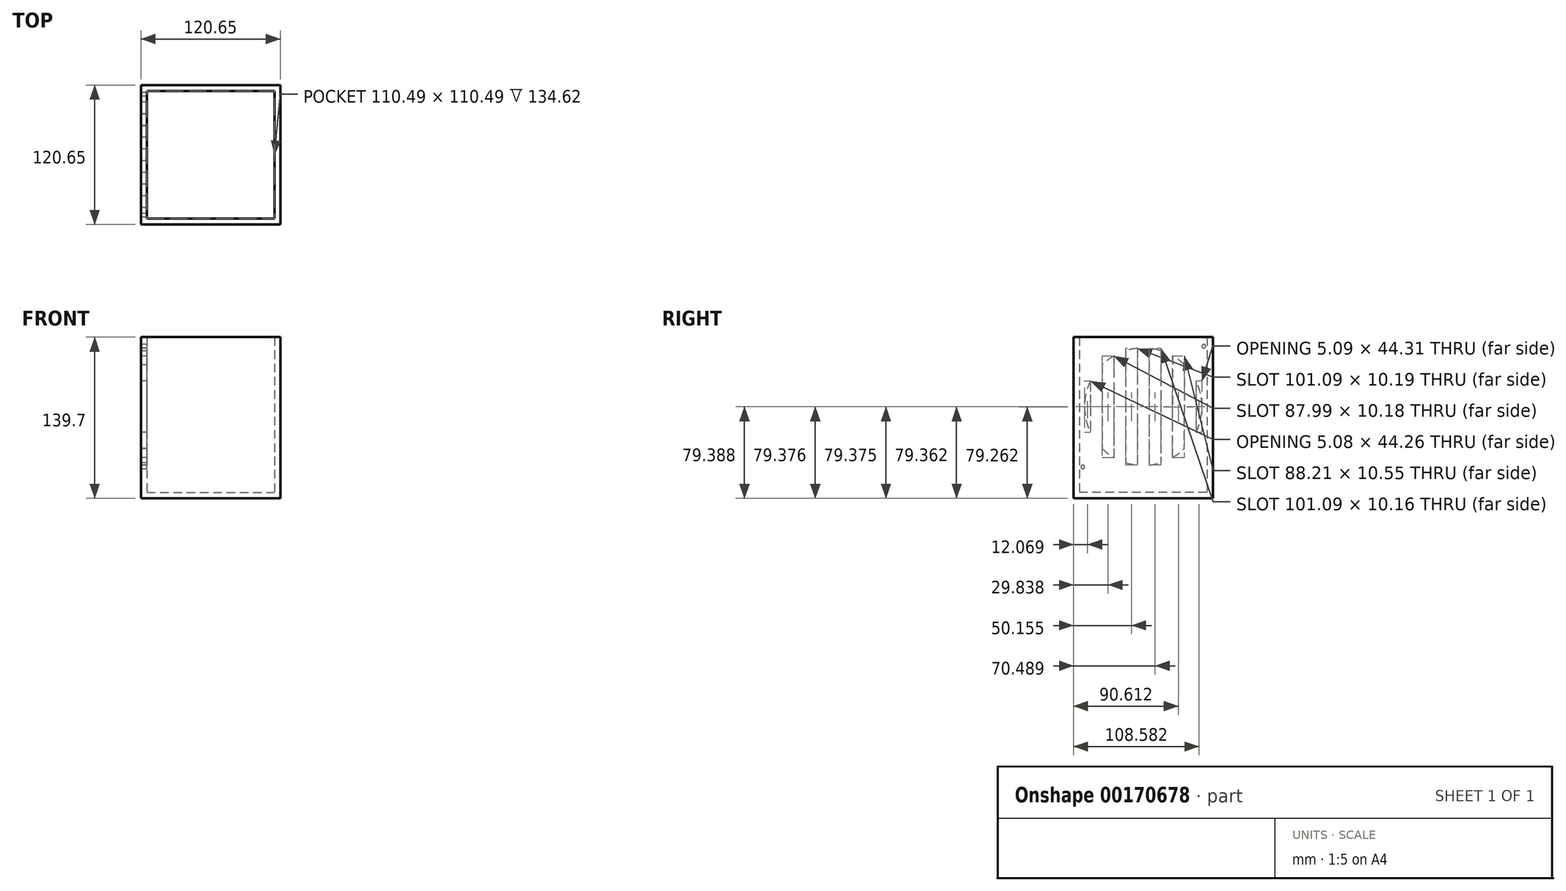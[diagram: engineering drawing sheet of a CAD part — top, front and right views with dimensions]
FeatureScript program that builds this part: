
annotation { "Feature Type Name" : "Feature", "Feature Type Description" : "" }
export const myFeature = defineFeature(function(context is Context, id is Id, definition is map)
    precondition{}
    {
        {
            var Q0;
            Q0=qCreatedBy(makeId("Top.planeOp"),FACE);
            var sketch = newSketch(context, id + "F0", { "sketchPlane" : qUnion([Q0])});
            skLineSegment(sketch, "E0.bottom", {"start": v(-81.61, 78.05) * mm, "end": v(39.04, 78.05) * mm});
            skLineSegment(sketch, "E0.top", {"start": v(-81.61, -42.6) * mm, "end": v(39.04, -42.6) * mm});
            skLineSegment(sketch, "E0.left", {"start": v(-81.61, 78.05) * mm, "end": v(-81.61, -42.6) * mm});
            skLineSegment(sketch, "E0.right", {"start": v(39.04, 78.05) * mm, "end": v(39.04, -42.6) * mm});
            skSolve(sketch);
        }
        {
            var Q0;
            Q0=makeQuery(id+"F0.imprint","IMPRINT",FACE,{"disambiguationData":[TD([[makeQuery(id+"F0.imprint","IMPRINT",EDGE,{"derivedFrom":sQuery(id+"F0.wireOp",EDGE,"E0.bottom")}),-1.0]])]});
            extrude(context, id + "F1", {"entities" : qUnion([Q0]), "depth" : 139.7 * mm});
        }
        {
            var Q0;
            Q0=makeQuery(id+"F1.opExtrude","CAP_FACE",FACE,{"disambiguationData":[OSD([sQuery(id+"F0.wireOp",EDGE,"E0.bottom"),sQuery(id+"F0.wireOp",EDGE,"E0.top"),sQuery(id+"F0.wireOp",EDGE,"E0.left"),sQuery(id+"F0.wireOp",EDGE,"E0.right")])],"isStart":false});
            shell(context, id + "F2", {"entities" : qUnion([Q0]), "thickness" : 5.08 * mm});
        }
        {
            var Q0;
            Q0=makeQuery(id+"F1.opExtrude","SWEPT_FACE",FACE,{"disambiguationData":[OSD([sQuery(id+"F0.wireOp",EDGE,"E0.left")])]});
            var sketch = newSketch(context, id + "F3", { "sketchPlane" : qUnion([Q0])});
            skCircle(sketch, "E1", {"center": v(-17.73, 79.38) * mm, "radius": 50.8 * mm});
            skPoint(sketch, "E1.centerSnap0", {"position": v(-17.73, 139.7) * mm});
            skLineSegment(sketch, "E2", {"start": v(-17.73, 130.18) * mm, "end": v(-17.7, 28.58) * mm});
            skPoint(sketch, "E3.startSnap0", {"position": v(-20.19, 79.42) * mm});
            skLineSegment(sketch, "E4", {"start": v(-17.73, 79.38) * mm, "end": v(-12.65, 79.38) * mm});
            skLineSegment(sketch, "E5", {"start": v(-12.65, 79.38) * mm, "end": v(-22.8, 79.42) * mm});
            skLineSegment(sketch, "E6", {"start": v(-22.8, 129.92) * mm, "end": v(-22.8, 28.83) * mm});
            skLineSegment(sketch, "E7", {"start": v(-12.65, 129.92) * mm, "end": v(-12.62, 28.83) * mm});
            skLineSegment(sketch, "E8", {"start": v(-22.8, 79.42) * mm, "end": v(-32.97, 79.42) * mm});
            skLineSegment(sketch, "E9", {"start": v(-32.97, 79.42) * mm, "end": v(-43.13, 79.42) * mm});
            skLineSegment(sketch, "E10", {"start": v(-43.13, 79.42) * mm, "end": v(-53.29, 79.38) * mm});
            skLineSegment(sketch, "E11", {"start": v(-53.29, 79.38) * mm, "end": v(-63.45, 79.37) * mm});
            skLineSegment(sketch, "E12", {"start": v(-63.45, 79.37) * mm, "end": v(-68.53, 79.37) * mm});
            skLineSegment(sketch, "E13", {"start": v(33.07, 79.38) * mm, "end": v(28, 79.38) * mm});
            skLineSegment(sketch, "E14", {"start": v(28, 79.38) * mm, "end": v(17.83, 79.37) * mm});
            skLineSegment(sketch, "E15", {"start": v(17.83, 79.37) * mm, "end": v(7.67, 79.37) * mm});
            skLineSegment(sketch, "E16", {"start": v(7.67, 79.37) * mm, "end": v(-2.49, 79.37) * mm});
            skLineSegment(sketch, "E17", {"start": v(-2.49, 79.37) * mm, "end": v(-12.65, 79.38) * mm});
            skLineSegment(sketch, "E18", {"start": v(-32.97, 127.84) * mm, "end": v(-32.97, 30.91) * mm});
            skLineSegment(sketch, "E19", {"start": v(-43.13, 123.37) * mm, "end": v(-42.73, 35.16) * mm});
            skLineSegment(sketch, "E20", {"start": v(-53.29, 115.65) * mm, "end": v(-52.96, 42.78) * mm});
            skLineSegment(sketch, "E21", {"start": v(-63.45, 101.52) * mm, "end": v(-63.44, 57.2) * mm});
            skLineSegment(sketch, "E22", {"start": v(-2.49, 127.84) * mm, "end": v(-2.46, 30.92) * mm});
            skLineSegment(sketch, "E23", {"start": v(7.67, 123.37) * mm, "end": v(7.67, 35.38) * mm});
            skLineSegment(sketch, "E24", {"start": v(17.83, 115.65) * mm, "end": v(17.85, 43.12) * mm});
            skLineSegment(sketch, "E25", {"start": v(28, 101.52) * mm, "end": v(28, 57.26) * mm});
            skSolve(sketch);
        }
        {
            var Q0;
            {var subQ5=sQuery(id+"F3.wireOp",EDGE,"E8");Q0=makeQuery(id+"F3.imprint","IMPRINT",FACE,{"disambiguationData":[TD([[makeQuery(id+"F3.imprint","IMPRINT",EDGE,{"derivedFrom":subQ5}),-1.0]])]});}
            var Q1;
            {var subQ5=sQuery(id+"F3.wireOp",EDGE,"E8");Q1=makeQuery(id+"F3.imprint","IMPRINT",FACE,{"disambiguationData":[TD([[makeQuery(id+"F3.imprint","IMPRINT",EDGE,{"derivedFrom":subQ5}),1.0]])]});}
            var Q2;
            {var subQ5=sQuery(id+"F3.wireOp",EDGE,"E7");var subQ6=sQuery(id+"F3.wireOp",EDGE,"E1");var subQ7=makeQuery(id+"F3.imprint","INTERSECT",VERTEX,{"disambiguationData":[OD(1.0)],"derivedFrom":[subQ6,subQ5]});Q2=makeQuery(id+"F3.imprint","IMPRINT",FACE,{"disambiguationData":[TD([[makeQuery(id+"F3.imprint","IMPRINT",EDGE,{"disambiguationData":[TD([[subQ7,-1.0]])],"derivedFrom":subQ6}),1.0]])]});}
            var Q3;
            {var subQ3=sQuery(id+"F3.wireOp",EDGE,"E7");var subQ6=sQuery(id+"F3.wireOp",EDGE,"E1");var subQ9=makeQuery(id+"F3.imprint","INTERSECT",VERTEX,{"disambiguationData":[OD(0.0)],"derivedFrom":[subQ6,subQ3]});Q3=makeQuery(id+"F3.imprint","IMPRINT",FACE,{"disambiguationData":[TD([[makeQuery(id+"F3.imprint","IMPRINT",EDGE,{"disambiguationData":[TD([[subQ9,1.0]])],"derivedFrom":subQ6}),1.0]])]});}
            var Q4;
            {var subQ0=sQuery(id+"F3.wireOp",EDGE,"E15");Q4=makeQuery(id+"F3.imprint","IMPRINT",FACE,{"disambiguationData":[TD([[makeQuery(id+"F3.imprint","IMPRINT",EDGE,{"derivedFrom":subQ0}),-1.0]])]});}
            var Q5;
            {var subQ1=sQuery(id+"F3.wireOp",EDGE,"E15");Q5=makeQuery(id+"F3.imprint","IMPRINT",FACE,{"disambiguationData":[TD([[makeQuery(id+"F3.imprint","IMPRINT",EDGE,{"derivedFrom":subQ1}),1.0]])]});}
            var Q6;
            {var subQ0=sQuery(id+"F3.wireOp",EDGE,"E13");var subQ1=sQuery(id+"F3.wireOp",EDGE,"E1");var subQ2=makeQuery(id+"F3.imprint","INTERSECT",VERTEX,{"derivedFrom":[subQ1,subQ0]});Q6=makeQuery(id+"F3.imprint","IMPRINT",FACE,{"disambiguationData":[TD([[makeQuery(id+"F3.imprint","IMPRINT",EDGE,{"disambiguationData":[TD([[subQ2,-1.0]])],"derivedFrom":subQ1}),1.0]])]});}
            var Q7;
            {var subQ0=sQuery(id+"F3.wireOp",EDGE,"E13");var subQ1=sQuery(id+"F3.wireOp",EDGE,"E1");var subQ2=makeQuery(id+"F3.imprint","INTERSECT",VERTEX,{"derivedFrom":[subQ1,subQ0]});Q7=makeQuery(id+"F3.imprint","IMPRINT",FACE,{"disambiguationData":[TD([[makeQuery(id+"F3.imprint","IMPRINT",EDGE,{"disambiguationData":[TD([[subQ2,1.0]])],"derivedFrom":subQ1}),1.0]])]});}
            var Q8;
            {var subQ5=sQuery(id+"F3.wireOp",EDGE,"E19");var subQ6=sQuery(id+"F3.wireOp",EDGE,"E1");var subQ7=makeQuery(id+"F3.imprint","INTERSECT",VERTEX,{"disambiguationData":[OD(0.0)],"derivedFrom":[subQ6,subQ5]});Q8=makeQuery(id+"F3.imprint","IMPRINT",FACE,{"disambiguationData":[TD([[makeQuery(id+"F3.imprint","IMPRINT",EDGE,{"disambiguationData":[TD([[subQ7,-1.0]])],"derivedFrom":subQ6}),1.0]])]});}
            var Q9;
            {var subQ0=sQuery(id+"F3.wireOp",EDGE,"E19");var subQ1=sQuery(id+"F3.wireOp",EDGE,"E1");var subQ2=makeQuery(id+"F3.imprint","INTERSECT",VERTEX,{"disambiguationData":[OD(1.0)],"derivedFrom":[subQ1,subQ0]});Q9=makeQuery(id+"F3.imprint","IMPRINT",FACE,{"disambiguationData":[TD([[makeQuery(id+"F3.imprint","IMPRINT",EDGE,{"disambiguationData":[TD([[subQ2,1.0]])],"derivedFrom":subQ1}),1.0]])]});}
            var Q10;
            {var subQ0=sQuery(id+"F3.wireOp",EDGE,"E12");Q10=makeQuery(id+"F3.imprint","IMPRINT",FACE,{"disambiguationData":[TD([[makeQuery(id+"F3.imprint","IMPRINT",EDGE,{"derivedFrom":subQ0}),-1.0]])]});}
            var Q11;
            {var subQ0=sQuery(id+"F3.wireOp",EDGE,"E12");Q11=makeQuery(id+"F3.imprint","IMPRINT",FACE,{"disambiguationData":[TD([[makeQuery(id+"F3.imprint","IMPRINT",EDGE,{"derivedFrom":subQ0}),1.0]])]});}
            extrude(context, id + "F4", {"entities" : qUnion([Q0, Q1, Q2, Q3, Q4, Q5, Q6, Q7, Q8, Q9, Q10, Q11]), "operationType" : NewBodyOperationType.REMOVE, "oppositeDirection" : true, "depth" : 25.4 * mm});
        }
        {
            var Q0;
            Q0=makeQuery(id+"F1.opExtrude","SWEPT_FACE",FACE,{"disambiguationData":[OSD([sQuery(id+"F0.wireOp",EDGE,"E0.left")])]});
            var sketch = newSketch(context, id + "F5", { "sketchPlane" : qUnion([Q0])});
            skLineSegment(sketch, "E26", {"start": v(42.6, 139.7) * mm, "end": v(42.6, 26.99) * mm});
            skCircle(sketch, "E27", {"center": v(-70.08, 131.76) * mm, "radius": 1.59 * mm});
            skCircle(sketch, "E28", {"center": v(34.66, 27.2) * mm, "radius": 1.59 * mm});
            skSolve(sketch);
        }
        {
            var Q0;
            Q0=makeQuery(id+"F5.imprint","IMPRINT",FACE,{"disambiguationData":[TD([[makeQuery(id+"F5.imprint","IMPRINT",EDGE,{"derivedFrom":sQuery(id+"F5.wireOp",EDGE,"E28")}),1.0]])]});
            var Q1;
            Q1=makeQuery(id+"F5.imprint","IMPRINT",FACE,{"disambiguationData":[TD([[makeQuery(id+"F5.imprint","IMPRINT",EDGE,{"derivedFrom":sQuery(id+"F5.wireOp",EDGE,"E27")}),1.0]])]});
            extrude(context, id + "F6", {"entities" : qUnion([Q0, Q1]), "operationType" : NewBodyOperationType.REMOVE, "oppositeDirection" : true, "depth" : 25.4 * mm});
        }
    });
